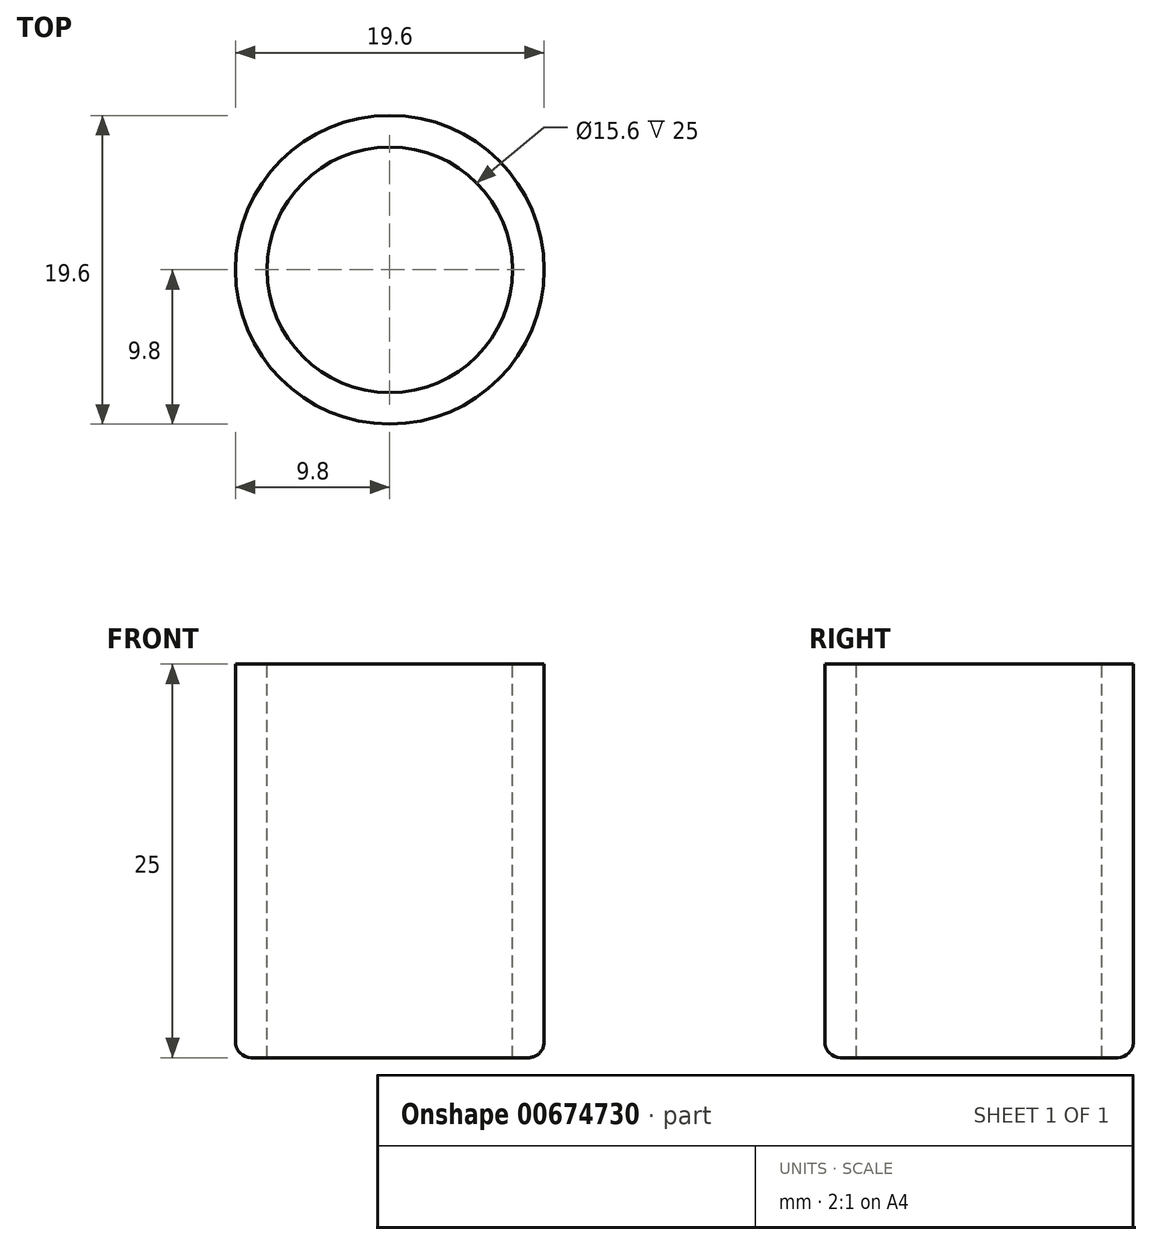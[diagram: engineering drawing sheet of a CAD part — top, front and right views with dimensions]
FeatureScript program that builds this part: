
annotation { "Feature Type Name" : "Feature", "Feature Type Description" : "" }
export const myFeature = defineFeature(function(context is Context, id is Id, definition is map)
    precondition{}
    {
        {
            var Q0;
            Q0=qCreatedBy(makeId("Top.planeOp"),FACE);
            var sketch = newSketch(context, id + "F0", { "sketchPlane" : qUnion([Q0])});
            skCircle(sketch, "E0", {"center": v(0, 0) * mm, "radius": 9.8 * mm});
            skCircle(sketch, "E1", {"center": v(0, 0) * mm, "radius": 7.8 * mm});
            skSolve(sketch);
        }
        {
            var Q0;
            Q0=makeQuery(id+"F0.imprint","IMPRINT",FACE,{"disambiguationData":[TD([[makeQuery(id+"F0.imprint","IMPRINT",EDGE,{"derivedFrom":sQuery(id+"F0.wireOp",EDGE,"E0")}),1.0]])]});
            extrude(context, id + "F1", {"entities" : qUnion([Q0]), "oppositeDirection" : true, "depth" : 25 * mm, "offsetDistance" : 25 * mm});
        }
        {
            var Q0;
            Q0=makeQuery(id+"F1.opExtrude","CAP_EDGE",EDGE,{"disambiguationData":[OSD([sQuery(id+"F0.wireOp",EDGE,"E0")])],"isStart":false});
            fillet(context, id + "F2", {"entities" : qUnion([Q0]), "radius" : 1 * mm, "tangentPropagation" : true, "allowEdgeOverflow" : false});
        }
    });
